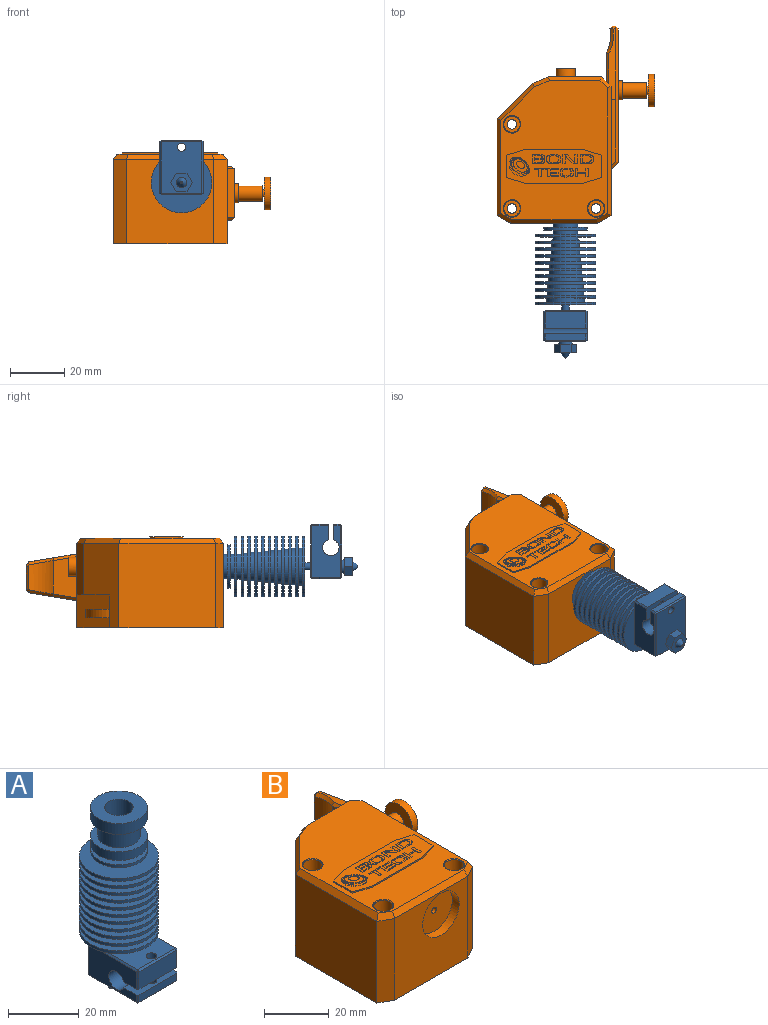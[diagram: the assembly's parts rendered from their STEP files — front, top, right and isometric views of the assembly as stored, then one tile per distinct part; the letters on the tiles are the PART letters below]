
ASSEMBLY  parts=2 mates=1
PART A: 111 faces, bbox 22.3x26.7x62.3 mm
  f0: cylinder r=8mm len=16mm, axis (0,0,1), area 186mm2, adj f1,f27
  f1: plane 16x16mm, normal (0,0,1), area 150.8mm2, adj f0,f2
  f2: cylinder r=4mm len=8mm, axis (0,0,1), area 163.4mm2, adj f1,f3
  f3: plane 8x8mm, normal (0,0,1), area 50.3mm2, adj f2
  f4: cylinder r=1.4mm len=2.8mm, axis (0,0,1), area 18.5mm2, adj f53,f95
  f5: plane 0.5x0.5mm, normal (-0.58,-0.58,0.58), area 0.2mm2, adj f13,f14,f98
  f6: plane 0.5x0.5mm, normal (-0.58,0.58,0.58), area 0.2mm2, adj f98,f100,f108
  f7: cylinder r=8mm len=16mm, axis (0,0,1), area 150.8mm2, adj f21,f84
  f8: plane 2x2mm, normal (1,0,0), area 1.3mm2, adj f38,f87
  f9: cylinder r=8mm len=16mm, axis (0,0,1), area 50.3mm2, adj f40,f82
  f10: plane 22.3x22.3mm, normal (0,0,-1), area 295.5mm2, adj f11,f51
  f11: cylinder r=11.15mm len=22.3mm, axis (0,0,1), area 70.1mm2, adj f10,f73
  f12: cylinder r=6.75mm len=13.5mm, axis (0,0,1), area 63.6mm2, adj f16,f64
  f13: plane 15x0.5mm, normal (0,-0.71,0.71), area 10.6mm2, adj f5,f95,f97,f110
  f14: plane 6x0.5mm, normal (-0.71,-0.71,0), area 4.2mm2, adj f5,f85,f96,f97
  f15: plane 3.5x3mm, normal (0.87,-0.5,0), area 12.1mm2, adj f34,f36,f89,f90
  f16: plane 22.3x22.3mm, normal (0,0,1), area 247.4mm2, adj f12,f50
  f17: cylinder r=1.5mm len=6.5mm, axis (0,0,1), area 61.3mm2, adj f95,f96
  f18: cylinder r=6mm len=12mm, axis (0,0,1), area 226.2mm2, adj f27,f84
  f19: cylinder r=11.15mm len=22.3mm, axis (0,0,1), area 70.1mm2, adj f26,f72
  f20: plane 0.5x0.5mm, normal (0.58,0.58,0.58), area 0.2mm2, adj f100,f104,f107
  f21: plane 16x16mm, normal (0,0,-1), area 137.4mm2, adj f7,f83
  f22: cylinder r=2.5mm len=5mm, axis (0,0,1), area 15.7mm2, adj f90,f94
  f23: cylinder r=4.75mm len=9.5mm, axis (0,0,1), area 44.8mm2, adj f25,f78
  f24: cylinder r=0.2mm len=3mm, axis (0,0,-1), area 3.8mm2, adj f56,f92
  f25: plane 22.3x22.3mm, normal (0,0,1), area 319.7mm2, adj f23,f30
  f26: plane 22.3x22.3mm, normal (0,0,-1), area 286.7mm2, adj f19,f71
  f27: plane 16x16mm, normal (0,0,-1), area 88mm2, adj f0,f18
  f28: plane 0.5x0.5mm, normal (-0.58,-0.58,-0.58), area 0.2mm2, adj f43,f102,f106
  f29: cylinder r=11.15mm len=22.3mm, axis (0,0,1), area 70.1mm2, adj f74,f75
  f30: cylinder r=11.15mm len=22.3mm, axis (0,0,1), area 70.1mm2, adj f25,f77
  f31: plane 19x0.5mm, normal (0.71,0,-0.71), area 13.4mm2, adj f49,f58,f94,f105
  f32: plane 4.04x3mm, normal (0,1,0), area 12.1mm2, adj f33,f34,f89,f90
  f33: plane 3.5x3mm, normal (-0.87,0.5,0), area 12.1mm2, adj f32,f35,f89,f90
  f34: plane 3.5x3mm, normal (0.87,0.5,0), area 12.1mm2, adj f15,f32,f89,f90
  f35: plane 3.5x3mm, normal (-0.87,-0.5,0), area 12.1mm2, adj f33,f36,f89,f90
  f36: plane 4.04x3mm, normal (0,-1,0), area 12.1mm2, adj f15,f35,f89,f90
  f37: plane 22.3x22.3mm, normal (0,0,1), area 267.9mm2, adj f42,f59
  f38: cylinder r=1mm len=2mm, axis (1,0,0), area 12.6mm2, adj f8,f58
  f39: cylinder r=7mm len=14mm, axis (0,0,1), area 66mm2, adj f47,f65
  f40: plane 16x16mm, normal (0,0,1), area 137.4mm2, adj f9,f83
  f41: cylinder r=11.15mm len=22.3mm, axis (0,0,1), area 70.1mm2, adj f45,f67
  f42: cylinder r=11.15mm len=22.3mm, axis (0,0,1), area 70.1mm2, adj f37,f60
  f43: plane 19x0.5mm, normal (-0.71,0,-0.71), area 13.4mm2, adj f28,f85,f94,f109
  f44: plane 16x5.65mm, normal (0,0,1), area 83mm2, adj f48,f57,f58,f85,f88,f103,f106
  f45: plane 22.3x22.3mm, normal (0,0,-1), area 267.9mm2, adj f41,f59
  f46: cylinder r=5.25mm len=10.5mm, axis (0,0,1), area 49.5mm2, adj f73,f74
  f47: plane 22.3x22.3mm, normal (0,0,-1), area 236.6mm2, adj f39,f50
  f48: plane 15x2.5mm, normal (0,-1,0), area 37.5mm2, adj f44,f102,f103,f106
  f49: plane 0.5x0.5mm, normal (0.58,-0.58,-0.58), area 0.2mm2, adj f31,f102,f103
  f50: cylinder r=11.15mm len=22.3mm, axis (0,0,1), area 70.1mm2, adj f16,f47
  f51: cylinder r=5.5mm len=11mm, axis (0,0,1), area 51.8mm2, adj f10,f72
  f52: cylinder r=6mm len=12mm, axis (0,0,1), area 56.5mm2, adj f67,f68
  f53: plane 22.3x22.3mm, normal (0,0,-1), area 384.4mm2, adj f4,f66
  f54: plane 3x3mm, normal (1,0,0), area 7.1mm2, adj f86
  f55: plane 1.55x1.55mm, normal (1,0,0), area 1.9mm2, adj f87
  f56: plane 0.4x0.4mm, normal (0,0,-1), area 0.1mm2, adj f24
  f57: cylinder r=3.02mm len=16mm, axis (1,0,0), area 271.5mm2, adj f44,f58,f85,f96
  f58: plane 19x10.5mm, normal (1,0,0), area 150.5mm2, adj f31,f38,f44,f57,f86,f96,f99,f103
  f59: cylinder r=6.25mm len=12.5mm, axis (0,0,1), area 58.9mm2, adj f37,f45
  f60: plane 22.3x22.3mm, normal (0,0,-1), area 257.8mm2, adj f42,f61
  f61: cylinder r=6.5mm len=13mm, axis (0,0,1), area 61.3mm2, adj f60,f62
  f62: plane 22.3x22.3mm, normal (0,0,1), area 257.8mm2, adj f61,f63
  f63: cylinder r=11.15mm len=22.3mm, axis (0,0,1), area 70.1mm2, adj f62,f64
  f64: plane 22.3x22.3mm, normal (0,0,-1), area 247.4mm2, adj f12,f63
  f65: plane 22.3x22.3mm, normal (0,0,1), area 236.6mm2, adj f39,f66
  f66: cylinder r=11.15mm len=22.3mm, axis (0,0,1), area 70.1mm2, adj f53,f65
  f67: plane 22.3x22.3mm, normal (0,0,1), area 277.5mm2, adj f41,f52
  f68: plane 22.3x22.3mm, normal (0,0,-1), area 277.5mm2, adj f52,f69
  f69: cylinder r=11.15mm len=22.3mm, axis (0,0,1), area 70.1mm2, adj f68,f70
  f70: plane 22.3x22.3mm, normal (0,0,1), area 286.7mm2, adj f69,f71
  f71: cylinder r=5.75mm len=11.5mm, axis (0,0,1), area 54.2mm2, adj f26,f70
  f72: plane 22.3x22.3mm, normal (0,0,1), area 295.5mm2, adj f19,f51
  f73: plane 22.3x22.3mm, normal (0,0,1), area 304mm2, adj f11,f46
  f74: plane 22.3x22.3mm, normal (0,0,-1), area 304mm2, adj f29,f46
  f75: plane 22.3x22.3mm, normal (0,0,1), area 312mm2, adj f29,f76
  f76: cylinder r=5mm len=10mm, axis (0,0,1), area 47.1mm2, adj f75,f77
  f77: plane 22.3x22.3mm, normal (0,0,-1), area 312mm2, adj f30,f76
  f78: plane 22.3x22.3mm, normal (0,0,-1), area 319.7mm2, adj f23,f79
  f79: cylinder r=11.15mm len=22.3mm, axis (0,0,1), area 70.1mm2, adj f78,f80
  f80: plane 22.3x22.3mm, normal (0,0,1), area 327mm2, adj f79,f81
  f81: cylinder r=4.5mm len=9mm, axis (0,0,1), area 42.4mm2, adj f80,f82
  f82: plane 16x16mm, normal (0,0,-1), area 137.4mm2, adj f9,f81
  f83: cylinder r=4.5mm len=9mm, axis (0,0,1), area 42.4mm2, adj f21,f40
  f84: plane 16x16mm, normal (0,0,1), area 88mm2, adj f7,f18
  f85: plane 19x10.5mm, normal (-1,0,0), area 160.7mm2, adj f14,f43,f44,f57,f96,f98,f106,f108
  f86: cylinder r=1.5mm len=3.45mm, axis (1,0,0), area 32.5mm2, adj f54,f58
  f87: cylinder r=0.78mm len=2.45mm, axis (1,0,0), area 11.9mm2, adj f8,f55
  f88: cylinder r=1.5mm len=3mm, axis (0,0,1), area 28.3mm2, adj f44,f94
  f89: plane 8.08x7mm, normal (0,0,-1), area 31.1mm2, adj f15,f32,f33,f34,f35,f36,f91
  f90: plane 8.08x7mm, normal (0,0,1), area 22.8mm2, adj f15,f22,f32,f33,f34,f35,f36
  f91: cone r=1.9mm half-angle=35deg, axis (0,0,1), area 18.4mm2, adj f89,f92
  f92: plane 1x1mm, normal (0,0,-1), area 0.7mm2, adj f24,f91
  f93: plane 15x10.5mm, normal (0,1,0), area 157.5mm2, adj f100,f101,f104,f108
  f94: plane 19x15mm, normal (0,0,-1), area 258.3mm2, adj f22,f31,f43,f88,f101,f102
  f95: plane 19x15mm, normal (0,0,1), area 271.8mm2, adj f4,f13,f17,f98,f100,f107
  f96: plane 16x5.65mm, normal (0,0,-1), area 83mm2, adj f14,f17,f57,f58,f85,f97,f99
  f97: plane 15x6mm, normal (0,-1,0), area 90mm2, adj f13,f14,f96,f99
  f98: plane 19x0.5mm, normal (-0.71,0,0.71), area 13.4mm2, adj f5,f6,f85,f95
  f99: plane 6x0.5mm, normal (0.71,-0.71,0), area 4.2mm2, adj f58,f96,f97,f110
  f100: plane 15x0.5mm, normal (0,0.71,0.71), area 10.6mm2, adj f6,f20,f93,f95
  f101: plane 15x0.5mm, normal (0,0.71,-0.71), area 10.6mm2, adj f93,f94,f105,f109
  f102: plane 15x0.5mm, normal (0,-0.71,-0.71), area 10.6mm2, adj f28,f48,f49,f94
  f103: plane 2.5x0.5mm, normal (0.71,-0.71,0), area 1.8mm2, adj f44,f48,f49,f58
  f104: plane 10.5x0.5mm, normal (0.71,0.71,0), area 7.4mm2, adj f20,f58,f93,f105
  f105: plane 0.5x0.5mm, normal (0.58,0.58,-0.58), area 0.2mm2, adj f31,f101,f104
  f106: plane 2.5x0.5mm, normal (-0.71,-0.71,0), area 1.8mm2, adj f28,f44,f48,f85
  f107: plane 19x0.5mm, normal (0.71,0,0.71), area 13.4mm2, adj f20,f58,f95,f110
  f108: plane 10.5x0.5mm, normal (-0.71,0.71,0), area 7.4mm2, adj f6,f85,f93,f109
  f109: plane 0.5x0.5mm, normal (-0.58,0.58,-0.58), area 0.2mm2, adj f43,f101,f108
  f110: plane 0.5x0.5mm, normal (0.58,-0.58,0.58), area 0.2mm2, adj f13,f99,f107
PART B: 276 faces, bbox 58.2x72.9x33.6 mm
  f0: cylinder r=13.85mm len=12.41mm, axis (0,0,1), area 103.3mm2, adj f33,f34,f35,f111,f116,f117,f118,f119
  f1: plane 1.54x0.1mm, normal (0,1,0), area 0.2mm2, adj f68,f152,f161,f167
  f2: plane 1.49x0.1mm, normal (0,1,0), area 0.1mm2, adj f176,f197,f253,f273
  f3: plane 35.61x31mm, normal (-1,0,0), area 1104mm2, adj f9,f23,f257,f258
  f4: cylinder r=1.75mm len=28.5mm, axis (0,0,1), area 313.4mm2, adj f136,f257
  f5: cylinder r=13mm len=17.46mm, axis (0,0,1), area 64.2mm2, adj f31,f139,f196,f200
  f6: cylinder r=1.75mm len=28.5mm, axis (0,0,1), area 313.4mm2, adj f135,f257
  f7: plane 3.9x3.15mm, normal (0,0,1), area 6.3mm2, adj f30,f181,f203,f211,f215,f216,f233,f234
  f8: plane 24.54x1.7mm, normal (0,0,1), area 40.3mm2, adj f113,f127,f128,f255
  f9: plane 35.61x2mm, normal (-0.82,0,0.57), area 85.3mm2, adj f3,f22,f180,f206
  f10: plane 1.84x0.1mm, normal (0,-1,0), area 0.2mm2, adj f94,f217,f219,f220
  f11: plane 6.55x1.8mm, normal (0,0,-1), area 10.2mm2, adj f112,f113,f201,f255
  f12: plane 8.82x1.26mm, normal (0,1,0), area 11.1mm2, adj f34,f35,f114,f115,f118,f124
  f13: cylinder r=1.75mm len=28.5mm, axis (0,0,1), area 313.4mm2, adj f137,f257
  f14: cone r=3mm half-angle=45deg, axis (0,0,1), area 6.9mm2, adj f206,f247
  f15: plane 3.15x0.1mm, normal (-1,0,0), area 0.3mm2, adj f217,f253,f268,f269
  f16: plane 0.9x0.1mm, normal (0,1,0), area 0.1mm2, adj f27,f29,f244,f253
  f17: plane 8.3x0.5mm, normal (1,0,0), area 4.2mm2, adj f19,f206,f253,f261
  f18: plane 3.07x0.1mm, normal (0,1,0), area 0.3mm2, adj f29,f240,f244,f253
  f19: plane 6.66x2mm, normal (0.29,-0.96,0), area 3.5mm2, adj f17,f206,f253,f260
  f20: plane 5.63x4.71mm, normal (0,0,1), area 1.5mm2, adj f36,f37,f38,f39,f40,f41,f42,f140
  f21: plane 1.4x0.1mm, normal (1,0,0), area 0.1mm2, adj f241,f242,f244,f253
  f22: plane 13.82x13.61mm, normal (-0.58,0.58,0.57), area 43.9mm2, adj f9,f23,f195,f206
  f23: plane 31x13.03mm, normal (-0.71,0.71,0), area 409.4mm2, adj f3,f22,f138,f174,f200,f257
  f24: plane 6.66x2mm, normal (-0.29,-0.96,0), area 3.5mm2, adj f206,f253,f260,f264
  f25: plane 0.9x0.1mm, normal (0,-1,0), area 0.1mm2, adj f177,f228,f232,f253
  f26: plane 3.1x2.91mm, normal (0,0,1), area 5.8mm2, adj f48,f49,f50,f145
  f27: plane 3.15x0.1mm, normal (-1,0,0), area 0.3mm2, adj f16,f241,f244,f253
  f28: cone r=3mm half-angle=45deg, axis (0,0,1), area 6.9mm2, adj f206,f210
  f29: plane 1.34x0.1mm, normal (1,0,0), area 0.1mm2, adj f16,f18,f244,f253
  f30: plane 0.94x0.1mm, normal (1,0,0), area 0.1mm2, adj f7,f233,f238,f253
  f31: plane 17.46x8.75mm, normal (0,0,-1), area 92.5mm2, adj f5,f196,f200
  f32: plane 25.81x4.29mm, normal (0,0.16,-0.99), area 59.8mm2, adj f33,f109,f110,f114,f119,f122,f201,f204
  f33: bspline ~9.42x2.69mm, area 13.7mm2, adj f0,f32,f35,f114,f119
  f34: bspline ~1.95x1.79mm, area 1.4mm2, adj f0,f12,f115,f117,f118
  f35: bspline ~1.96x1.86mm, area 1.4mm2, adj f0,f12,f33,f114,f118
  f36: extruded ~1.11x0.12mm, area 0.1mm2, adj f20,f42,f140,f253
  f37: extruded ~1.46x0.61mm, area 0.2mm2, adj f20,f38,f140,f253
  f38: extruded ~2.8x1.93mm, area 0.4mm2, adj f20,f37,f39,f253
  f39: extruded ~2.12x0.3mm, area 0.2mm2, adj f20,f38,f141,f253
  f40: extruded ~2.24x0.4mm, area 0.2mm2, adj f20,f41,f141,f253
  f41: cylinder r=5.04mm len=1.92mm, axis (0,0,-1), area 0.3mm2, adj f20,f40,f42,f253
  f42: extruded ~1.55x0.73mm, area 0.2mm2, adj f20,f36,f41,f253
  f43: extruded ~1.38x0.67mm, area 0.2mm2, adj f44,f142,f143,f253
  f44: extruded ~2.07x1.1mm, area 0.2mm2, adj f43,f45,f142,f253
  f45: extruded ~2.25x1.17mm, area 0.3mm2, adj f44,f142,f144,f253
  f46: extruded ~1.64x0.27mm, area 0.2mm2, adj f47,f142,f144,f253
  f47: extruded ~2.81x2.58mm, area 0.4mm2, adj f46,f142,f143,f253
  f48: extruded ~1.83x1.74mm, area 0.3mm2, adj f26,f50,f142,f145
  f49: extruded ~1.65x1.53mm, area 0.2mm2, adj f26,f50,f142,f145
  f50: extruded ~1.24x0.98mm, area 0.2mm2, adj f26,f48,f49,f142
  f51: extruded ~2.04x0.25mm, area 0.2mm2, adj f57,f146,f148,f253
  f52: extruded ~1.54x0.45mm, area 0.2mm2, adj f53,f146,f148,f253
  f53: extruded ~1.53x1.38mm, area 0.2mm2, adj f52,f54,f148,f253
  f54: extruded ~2.62x1.38mm, area 0.3mm2, adj f53,f147,f148,f253
  f55: extruded ~1.29x0.51mm, area 0.1mm2, adj f56,f147,f148,f253
  f56: extruded ~1.46x0.16mm, area 0.1mm2, adj f55,f57,f148,f253
  f57: cylinder r=4.69mm len=0.71mm, axis (0,0,-1), area 0.1mm2, adj f51,f56,f148,f253
  f58: extruded ~2.39x1.09mm, area 0.3mm2, adj f59,f149,f151,f253
  f59: extruded ~2.4x1.57mm, area 0.3mm2, adj f58,f60,f151,f253
  f60: cylinder r=4.22mm len=0.95mm, axis (0,0,-1), area 0.1mm2, adj f59,f150,f151,f253
  f61: extruded ~1.7x0.45mm, area 0.2mm2, adj f62,f150,f151,f253
  f62: extruded ~2.49x0.99mm, area 0.3mm2, adj f61,f63,f151,f253
  f63: extruded ~1.82x0.79mm, area 0.2mm2, adj f62,f149,f151,f253
  f64: extruded ~1.11x0.11mm, area 0.1mm2, adj f65,f152,f156,f253
  f65: extruded ~0.77x0.59mm, area 0.1mm2, adj f64,f66,f152,f253
  f66: extruded ~0.97x0.75mm, area 0.1mm2, adj f65,f152,f157,f253
  f67: extruded ~0.72x0.52mm, area 0.1mm2, adj f152,f153,f158,f253
  f68: extruded ~0.88x0.1mm, area 0.1mm2, adj f1,f69,f152,f167
  f69: extruded ~0.43x0.28mm, area 0.1mm2, adj f68,f152,f159,f167
  f70: extruded ~0.62x0.1mm, area 0.1mm2, adj f152,f159,f160,f167
  f71: extruded ~1.25x0.1mm, area 0.1mm2, adj f72,f152,f165,f166
  f72: extruded ~0.42x0.3mm, area 0.1mm2, adj f71,f152,f162,f166
  f73: extruded ~0.94x0.1mm, area 0.1mm2, adj f152,f162,f163,f166
  f74: extruded ~2.17x0.35mm, area 0.2mm2, adj f75,f168,f170,f253
  f75: extruded ~0.8x0.55mm, area 0.1mm2, adj f74,f168,f169,f253
  f76: extruded ~0.83x0.56mm, area 0.1mm2, adj f77,f168,f169,f253
  f77: extruded ~1.73x0.11mm, area 0.2mm2, adj f76,f78,f168,f253
  f78: extruded ~0.83x0.7mm, area 0.1mm2, adj f77,f168,f170,f253
  f79: extruded ~0.66x0.42mm, area 0.1mm2, adj f80,f168,f271,f272
  f80: extruded ~1.32x0.1mm, area 0.1mm2, adj f79,f81,f168,f272
  f81: extruded ~1.47x0.33mm, area 0.2mm2, adj f80,f168,f171,f272
  f82: extruded ~1.05x0.28mm, area 0.1mm2, adj f83,f168,f171,f272
  f83: extruded ~1.38x0.14mm, area 0.1mm2, adj f82,f84,f168,f272
  f84: extruded ~1.28x0.1mm, area 0.1mm2, adj f83,f168,f172,f272
  f85: cylinder r=75.43mm len=0.81mm, axis (0,0,-1), area 0.1mm2, adj f175,f176,f253,f275
  f86: cylinder r=23.29mm len=0.65mm, axis (0,0,-1), area 0.1mm2, adj f176,f192,f207,f253
  f87: cylinder r=46mm len=1.01mm, axis (0,0,-1), area 0.1mm2, adj f176,f192,f197,f253
  f88: extruded ~1.65x0.27mm, area 0.2mm2, adj f91,f217,f253,f268
  f89: cylinder r=6.11mm len=0.81mm, axis (0,0,-1), area 0.1mm2, adj f90,f217,f253,f269
  f90: extruded ~0.98x0.4mm, area 0.1mm2, adj f89,f217,f253,f270
  f91: extruded ~1.1x0.54mm, area 0.1mm2, adj f88,f217,f253,f270
  f92: extruded ~1.15x0.19mm, area 0.1mm2, adj f93,f193,f217,f220
  f93: extruded ~0.94x0.29mm, area 0.1mm2, adj f92,f217,f218,f220
  f94: extruded ~1.07x0.19mm, area 0.1mm2, adj f10,f217,f218,f220
  f95: extruded ~0.78x0.36mm, area 0.1mm2, adj f183,f213,f227,f253
  f96: cylinder r=0.76mm len=0.15mm, axis (0,0,1), area 0mm2, adj f183,f221,f222,f253
  f97: extruded ~1.33x0.25mm, area 0.1mm2, adj f98,f183,f222,f253
  f98: extruded ~1.24x0.16mm, area 0.1mm2, adj f97,f99,f183,f253
  f99: extruded ~0.77x0.26mm, area 0.1mm2, adj f98,f183,f223,f253
  f100: extruded ~1.06x0.16mm, area 0.1mm2, adj f101,f183,f223,f253
  f101: extruded ~0.46x0.13mm, area 0mm2, adj f100,f183,f224,f253
  f102: cylinder r=2.28mm len=0.35mm, axis (0,0,-1), area 0mm2, adj f183,f224,f225,f253
  f103: extruded ~1.4x0.12mm, area 0.1mm2, adj f104,f183,f225,f253
  f104: extruded ~1.29x0.1mm, area 0.1mm2, adj f103,f105,f183,f253
  f105: extruded ~1.31x0.48mm, area 0.1mm2, adj f104,f183,f226,f253
  f106: extruded ~0.86x0.1mm, area 0.1mm2, adj f107,f183,f226,f253
  f107: extruded ~0.87x0.61mm, area 0.1mm2, adj f106,f108,f183,f253
  f108: extruded ~1.77x0.18mm, area 0.2mm2, adj f107,f183,f227,f253
  f109: plane 6.55x1.09mm, normal (1,0,0), area 3.6mm2, adj f32,f110,f201
  f110: plane 6.55x1.8mm, normal (0,0,1), area 10.2mm2, adj f32,f109,f201,f255
  f111: plane 15.8x10.33mm, normal (-1,0,0), area 145.5mm2, adj f0,f116,f119,f201
  f112: plane 6.55x1.09mm, normal (1,0,0), area 3.6mm2, adj f11,f113,f201
  f113: plane 26.02x4.33mm, normal (0,0.16,0.99), area 60mm2, adj f8,f11,f112,f115,f116,f117,f126,f201
  f114: plane 1.23x1.2mm, normal (0,0.71,-0.71), area 1.9mm2, adj f12,f32,f33,f35,f123
  f115: plane 1.38x1.24mm, normal (0,0.81,0.58), area 1.9mm2, adj f12,f34,f113,f117,f125
  f116: plane 11.38x2.9mm, normal (-0.71,0.12,0.7), area 15.5mm2, adj f0,f111,f113,f117,f201
  f117: bspline ~9.52x2.69mm, area 13.8mm2, adj f0,f34,f113,f115,f116
  f118: plane 8.79x0.84mm, normal (-0.71,0.71,0), area 9.7mm2, adj f0,f12,f34,f35
  f119: plane 11.38x2.9mm, normal (-0.71,0.12,-0.7), area 15.5mm2, adj f0,f32,f33,f111,f201
  f120: plane 3.11x2.7mm, normal (0.5,-0.5,-0.71), area 4.4mm2, adj f121,f204,f255,f266
  f121: plane 23.25x1mm, normal (0.71,0,-0.71), area 32.5mm2, adj f120,f122,f204,f267
  f122: plane 25.88x5.22mm, normal (0.71,0.12,-0.7), area 36.7mm2, adj f32,f121,f123,f267
  f123: plane 1.68x1.61mm, normal (0.71,0.5,-0.5), area 1.9mm2, adj f114,f122,f124,f267
  f124: plane 8.82x1mm, normal (0.71,0.71,0), area 12mm2, adj f12,f123,f125,f267
  f125: plane 1.7x1.56mm, normal (0.71,0.58,0.41), area 1.9mm2, adj f115,f124,f126,f267
  f126: plane 26.09x5.24mm, normal (0.71,0.12,0.7), area 36.9mm2, adj f113,f125,f127,f267
  f127: plane 23.25x1mm, normal (0.71,0,0.71), area 32.5mm2, adj f8,f126,f128,f267
  f128: plane 3.11x2.7mm, normal (0.5,-0.5,0.71), area 4.4mm2, adj f8,f127,f255,f266
  f129: plane 7x7mm, normal (1,0,0), area 12.5mm2, adj f191,f250
  f130: plane 5.75x5.75mm, normal (1,0,0), area 16.3mm2, adj f191,f248
  f131: plane 12x12mm, normal (1,0,0), area 113.1mm2, adj f187
  f132: plane 12x12mm, normal (-1,0,0), area 106mm2, adj f187,f249
  f133: plane 3.5x3.5mm, normal (1,0,0), area 2.6mm2, adj f248,f249
  f134: plane 22x22mm, normal (0,0,-1), area 380.1mm2, adj f185
  f135: plane 6x6mm, normal (0,0,1), area 18.7mm2, adj f6,f247
  f136: plane 6x6mm, normal (0,0,1), area 18.7mm2, adj f4,f210
  f137: plane 6x6mm, normal (0,0,1), area 18.7mm2, adj f13,f246
  f138: plane 27x12mm, normal (0,0,-1), area 175.7mm2, adj f23,f174,f196,f200,f256
  f139: plane 17.46x8.75mm, normal (0,0,1), area 92.5mm2, adj f5,f196,f200
  f140: cylinder r=3.23mm len=0.75mm, axis (0,0,-1), area 0.1mm2, adj f20,f36,f37,f253
  f141: cylinder r=2.26mm len=0.61mm, axis (0,0,-1), area 0.1mm2, adj f20,f39,f40,f253
  f142: plane 5.29x4.97mm, normal (0,0,1), area 12.8mm2, adj f43,f44,f45,f46,f47,f48,f49,f50
  f143: extruded ~1.65x0.26mm, area 0.2mm2, adj f43,f47,f142,f253
  f144: extruded ~1.59x0.62mm, area 0.2mm2, adj f45,f46,f142,f253
  f145: extruded ~1.18x1.1mm, area 0.2mm2, adj f26,f48,f49,f142
  f146: extruded ~1.51x1mm, area 0.2mm2, adj f51,f52,f148,f253
  f147: extruded ~1.35x0.54mm, area 0.1mm2, adj f54,f55,f148,f253
  f148: plane 4.88x3.75mm, normal (0,0,1), area 2.3mm2, adj f51,f52,f53,f54,f55,f56,f57,f146
  f149: extruded ~1.42x0.34mm, area 0.1mm2, adj f58,f63,f151,f253
  f150: extruded ~3.9x2.5mm, area 0.5mm2, adj f60,f61,f151,f253
  f151: plane 7.09x3.47mm, normal (0,0,1), area 5.7mm2, adj f58,f59,f60,f61,f62,f63,f149,f150
  f152: plane 4.65x3.15mm, normal (0,0,1), area 8.6mm2, adj f1,f64,f65,f66,f67,f68,f69,f70
  f153: extruded ~1.23x0.11mm, area 0.1mm2, adj f67,f152,f154,f253
  f154: plane 2.74x0.1mm, normal (0,1,0), area 0.3mm2, adj f152,f153,f155,f253
  f155: plane 3.15x0.1mm, normal (-1,0,0), area 0.3mm2, adj f152,f154,f156,f253
  f156: plane 2.95x0.1mm, normal (0,-1,0), area 0.3mm2, adj f64,f152,f155,f253
  f157: plane 0.1x0.01mm, normal (1,0,0), area 0mm2, adj f66,f152,f158,f253
  f158: extruded ~0.81x0.68mm, area 0.1mm2, adj f67,f152,f157,f253
  f159: extruded ~0.42x0.33mm, area 0.1mm2, adj f69,f70,f152,f167
  f160: plane 1.75x0.1mm, normal (0,-1,0), area 0.2mm2, adj f70,f152,f161,f167
  f161: plane 0.95x0.1mm, normal (1,0,0), area 0.1mm2, adj f1,f152,f160,f167
  f162: extruded ~0.48x0.36mm, area 0.1mm2, adj f72,f73,f152,f166
  f163: plane 1.55x0.1mm, normal (0,-1,0), area 0.2mm2, adj f73,f152,f164,f166
  f164: plane 1.01x0.1mm, normal (1,0,0), area 0.1mm2, adj f152,f163,f165,f166
  f165: plane 1.31x0.1mm, normal (0,1,0), area 0.1mm2, adj f71,f152,f164,f166
  f166: plane 2.85x1.01mm, normal (0,0,1), area 2.8mm2, adj f71,f72,f73,f162,f163,f164,f165
  f167: plane 2.7x0.95mm, normal (0,0,1), area 2.5mm2, adj f1,f68,f69,f70,f159,f160,f161
  f168: plane 5.11x3.21mm, normal (0,0,1), area 7.5mm2, adj f74,f75,f76,f77,f78,f79,f80,f81
  f169: extruded ~3.27x0.11mm, area 0.3mm2, adj f75,f76,f168,f253
  f170: extruded ~3.87x0.37mm, area 0.4mm2, adj f74,f78,f168,f253
  f171: extruded ~0.87x0.1mm, area 0.1mm2, adj f81,f82,f168,f272
  f172: extruded ~0.65x0.36mm, area 0.1mm2, adj f84,f168,f271,f272
  f173: plane 5.38x3.7mm, normal (0.41,-0.71,0.57), area 12.7mm2, adj f184,f202,f206,f214
  f174: plane 19x5.98mm, normal (-0.38,0.92,0), area 122.9mm2, adj f23,f138,f195,f256
  f175: plane 2.06x1.93mm, normal (-0.68,-0.73,0), area 0.3mm2, adj f85,f176,f212,f253
  f176: plane 5.23x3.15mm, normal (0,0,1), area 8.8mm2, adj f2,f85,f86,f87,f175,f178,f192,f197
  f177: plane 4.51x3.15mm, normal (0,0,1), area 4.4mm2, adj f25,f189,f190,f228,f229,f230,f231,f232
  f178: plane 2.08x0.1mm, normal (1,0,0), area 0.2mm2, adj f176,f199,f253,f274
  f179: plane 4x4mm, normal (0,1,0), area 9.4mm2, adj f251,f252
  f180: plane 5.38x3.7mm, normal (-0.41,-0.71,0.57), area 12.7mm2, adj f9,f202,f206,f258
  f181: plane 1.03x0.1mm, normal (1,0,0), area 0.1mm2, adj f7,f216,f236,f253
  f182: plane 0.9x0.1mm, normal (0,1,0), area 0.1mm2, adj f239,f240,f244,f253
  f183: plane 4.84x3.21mm, normal (0,0,1), area 6.6mm2, adj f95,f96,f97,f98,f99,f100,f101,f102
  f184: plane 31x5mm, normal (0.5,-0.87,0), area 179mm2, adj f173,f254,f255,f257
  f185: cylinder r=11mm len=22mm, axis (0,0,1), area 138.2mm2, adj f134,f257
  f186: plane 1.4x0.1mm, normal (-1,0,0), area 0.1mm2, adj f242,f243,f244,f253
  f187: cylinder r=6mm len=12mm, axis (1,0,0), area 94.2mm2, adj f131,f132
  f188: plane 19.5x2mm, normal (0,0.82,0.57), area 46.6mm2, adj f195,f206,f256,f259
  f189: plane 1.82x0.1mm, normal (0,-1,0), area 0.2mm2, adj f177,f190,f228,f253
  f190: plane 0.44x0.1mm, normal (1,0,0), area 0mm2, adj f177,f189,f229,f253
  f191: cylinder r=2.88mm len=9mm, axis (1,0,0), area 162.6mm2, adj f129,f130
  f192: plane 0.1x0.03mm, normal (0,1,0), area 0mm2, adj f86,f87,f176,f253
  f193: plane 1.74x0.1mm, normal (0,1,0), area 0.2mm2, adj f92,f217,f219,f220
  f194: cylinder r=3.5mm len=7mm, axis (0,1,0), area 66mm2, adj f209,f256
  f195: plane 6.25x3.66mm, normal (-0.31,0.76,0.57), area 15.1mm2, adj f22,f174,f188,f206
  f196: plane 12x12mm, normal (-0.71,0.71,0), area 171.1mm2, adj f5,f31,f138,f139,f200,f256,f257
  f197: plane 1.82x1.74mm, normal (0.69,0.72,0), area 0.3mm2, adj f2,f87,f176,f253
  f198: plane 0.9x0.1mm, normal (0,1,0), area 0.1mm2, adj f176,f205,f207,f253
  f199: plane 0.89x0.1mm, normal (0,-1,0), area 0.1mm2, adj f176,f178,f253,f273
  f200: plane 15x12mm, normal (0,1,0), area 150.6mm2, adj f5,f23,f31,f138,f139,f196,f257
  f201: plane 31x3.5mm, normal (0.71,0.71,0), area 104mm2, adj f11,f32,f109,f110,f111,f112,f113,f116
  f202: plane 32x2mm, normal (0,-0.82,0.57), area 77.2mm2, adj f173,f180,f206,f254
  f203: plane 0.41x0.1mm, normal (1,0,0), area 0mm2, adj f7,f211,f236,f253
  f204: plane 24.54x1.7mm, normal (0,0,-1), area 40.3mm2, adj f32,f120,f121,f255
  f205: plane 3.15x0.1mm, normal (1,0,0), area 0.3mm2, adj f176,f198,f212,f253
  f206: plane 51.2x39.2mm, normal (0,0,1), area 1375.8mm2, adj f9,f14,f17,f19,f22,f24,f28,f173
  f207: plane 2.1x0.1mm, normal (-1,0,0), area 0.2mm2, adj f86,f176,f198,f253
  f208: cylinder r=8mm len=16mm, axis (0,1,0), area 150.8mm2, adj f254,f265
  f209: plane 7x7mm, normal (0,1,0), area 25.9mm2, adj f194,f251
  f210: cylinder r=3mm len=6mm, axis (0,0,-1), area 80.1mm2, adj f28,f136
  f211: plane 3.9x0.1mm, normal (0,-1,0), area 0.4mm2, adj f7,f203,f215,f253
  f212: plane 1.5x0.1mm, normal (0,-1,0), area 0.2mm2, adj f175,f176,f205,f253
  f213: plane 0.11x0.1mm, normal (1,0,0), area 0mm2, adj f95,f183,f221,f253
  f214: plane 47.61x2mm, normal (0.82,0,0.57), area 114.6mm2, adj f173,f206,f255,f259
  f215: plane 3.15x0.1mm, normal (-1,0,0), area 0.3mm2, adj f7,f211,f235,f253
  f216: plane 2.85x0.1mm, normal (0,-1,0), area 0.3mm2, adj f7,f181,f237,f253
  f217: plane 4.98x3.15mm, normal (0,0,1), area 7.9mm2, adj f10,f15,f88,f89,f90,f91,f92,f93
  f218: extruded ~0.99x0.27mm, area 0.1mm2, adj f93,f94,f217,f220
  f219: plane 2.32x0.1mm, normal (1,0,0), area 0.2mm2, adj f10,f193,f217,f220
  f220: plane 3.18x2.32mm, normal (0,0,1), area 7mm2, adj f10,f92,f93,f94,f193,f218,f219
  f221: plane 0.9x0.1mm, normal (0,1,0), area 0.1mm2, adj f96,f183,f213,f253
  f222: extruded ~1.53x0.55mm, area 0.2mm2, adj f96,f97,f183,f253
  f223: extruded ~1.48x0.13mm, area 0.1mm2, adj f99,f100,f183,f253
  f224: plane 0.9x0.1mm, normal (0,-1,0), area 0.1mm2, adj f101,f102,f183,f253
  f225: extruded ~0.57x0.56mm, area 0.1mm2, adj f102,f103,f183,f253
  f226: extruded ~0.79x0.18mm, area 0.1mm2, adj f105,f106,f183,f253
  f227: extruded ~2.07x0.23mm, area 0.2mm2, adj f95,f108,f183,f253
  f228: plane 2.72x0.1mm, normal (1,0,0), area 0.3mm2, adj f25,f177,f189,f253
  f229: plane 4.51x0.1mm, normal (0,1,0), area 0.5mm2, adj f177,f190,f230,f253
  f230: plane 0.44x0.1mm, normal (-1,0,0), area 0mm2, adj f177,f229,f231,f253
  f231: plane 1.79x0.1mm, normal (0,-1,0), area 0.2mm2, adj f177,f230,f232,f253
  f232: plane 2.72x0.1mm, normal (-1,0,0), area 0.3mm2, adj f25,f177,f231,f253
  f233: plane 2.99x0.1mm, normal (0,-1,0), area 0.3mm2, adj f7,f30,f234,f253
  f234: plane 0.41x0.1mm, normal (1,0,0), area 0mm2, adj f7,f233,f235,f253
  f235: plane 3.88x0.1mm, normal (0,1,0), area 0.4mm2, adj f7,f215,f234,f253
  f236: plane 3x0.1mm, normal (0,1,0), area 0.3mm2, adj f7,f181,f203,f253
  f237: plane 0.37x0.1mm, normal (1,0,0), area 0mm2, adj f7,f216,f238,f253
  f238: plane 2.85x0.1mm, normal (0,1,0), area 0.3mm2, adj f7,f30,f237,f253
  f239: plane 3.15x0.1mm, normal (1,0,0), area 0.3mm2, adj f182,f243,f244,f253
  f240: plane 1.34x0.1mm, normal (-1,0,0), area 0.1mm2, adj f18,f182,f244,f253
  f241: plane 0.9x0.1mm, normal (0,-1,0), area 0.1mm2, adj f21,f27,f244,f253
  f242: plane 3.07x0.1mm, normal (0,-1,0), area 0.3mm2, adj f21,f186,f244,f253
  f243: plane 0.9x0.1mm, normal (0,-1,0), area 0.1mm2, adj f186,f239,f244,f253
  f244: plane 4.86x3.15mm, normal (0,0,1), area 6.9mm2, adj f16,f18,f21,f27,f29,f182,f186,f239
  f245: cone r=3mm half-angle=45deg, axis (0,0,1), area 6.9mm2, adj f206,f246
  f246: cylinder r=3mm len=6mm, axis (0,0,-1), area 80.1mm2, adj f137,f245
  f247: cylinder r=3mm len=6mm, axis (0,0,-1), area 80.1mm2, adj f14,f135
  f248: cylinder r=1.75mm len=10.5mm, axis (1,0,0), area 115.5mm2, adj f130,f133
  f249: cylinder r=1.5mm len=11mm, axis (1,0,0), area 103.7mm2, adj f132,f133
  f250: cylinder r=3.5mm len=7mm, axis (1,0,0), area 33mm2, adj f129,f267
  f251: cylinder r=2mm len=4mm, axis (0,1,0), area 37.7mm2, adj f179,f209
  f252: cylinder r=1mm len=51mm, axis (0,1,0), area 320.4mm2, adj f179,f265
  f253: plane 35.32x12.32mm, normal (0,0,1), area 302.9mm2, adj f2,f15,f16,f17,f18,f19,f21,f24
  f254: plane 32x31mm, normal (0,-1,0), area 790.9mm2, adj f184,f202,f208,f257,f258
  f255: plane 47.61x31mm, normal (1,0,0), area 863.4mm2, adj f8,f11,f110,f120,f128,f184,f201,f204
  f256: plane 31x19.5mm, normal (0,1,0), area 428mm2, adj f138,f174,f188,f194,f196,f201,f257
  f257: plane 54x42mm, normal (0,0,-1), area 1538.3mm2, adj f3,f4,f6,f13,f23,f184,f185,f196
  f258: plane 31x5mm, normal (-0.5,-0.87,0), area 179mm2, adj f3,f180,f254,f257
  f259: plane 4.08x4.08mm, normal (0.58,0.58,0.57), area 10.7mm2, adj f188,f201,f206,f214
  f260: plane 21.99x0.5mm, normal (0,-1,0), area 11mm2, adj f19,f24,f206,f253
  f261: plane 6.66x2mm, normal (0.29,0.96,0), area 3.5mm2, adj f17,f206,f253,f262
  f262: plane 21.99x0.5mm, normal (0,1,0), area 11mm2, adj f206,f253,f261,f263
  f263: plane 6.66x2mm, normal (-0.29,0.96,0), area 3.5mm2, adj f206,f253,f262,f264
  f264: plane 8.3x0.5mm, normal (-1,0,0), area 4.2mm2, adj f24,f206,f253,f263
  f265: plane 16x16mm, normal (0,-1,0), area 197.9mm2, adj f208,f252
  f266: plane 18x2.7mm, normal (0.71,-0.71,0), area 68.7mm2, adj f120,f128,f255,f267
  f267: plane 49.25x18mm, normal (1,0,0), area 734.7mm2, adj f121,f122,f123,f124,f125,f126,f127,f250
  f268: plane 2.79x0.1mm, normal (0,1,0), area 0.3mm2, adj f15,f88,f217,f253
  f269: plane 2.9x0.1mm, normal (0,-1,0), area 0.3mm2, adj f15,f89,f217,f253
  f270: extruded ~1.33x0.29mm, area 0.1mm2, adj f90,f91,f217,f253
  f271: plane 0.88x0.1mm, normal (-1,0,0), area 0.1mm2, adj f79,f168,f172,f272
  f272: plane 3.31x2.38mm, normal (0,0,1), area 7.4mm2, adj f79,f80,f81,f82,f83,f84,f171,f172
  f273: plane 3.15x0.1mm, normal (-1,0,0), area 0.3mm2, adj f2,f176,f199,f253
  f274: cylinder r=11.16mm len=0.66mm, axis (0,0,-1), area 0.1mm2, adj f176,f178,f253,f275
  f275: plane 0.1x0.04mm, normal (0,-1,0), area 0mm2, adj f85,f176,f253,f274
PLACE A rot(axis=(-1,0,0),90deg) t=(-5.56,-71.14,29.44)mm
PLACE B t=(-9.81,-0.54,6.94)mm
MATE fastened A.f4 <-> B.f194  axis (0,-1,0) through (-5.56,-21.54,29.44)mm
